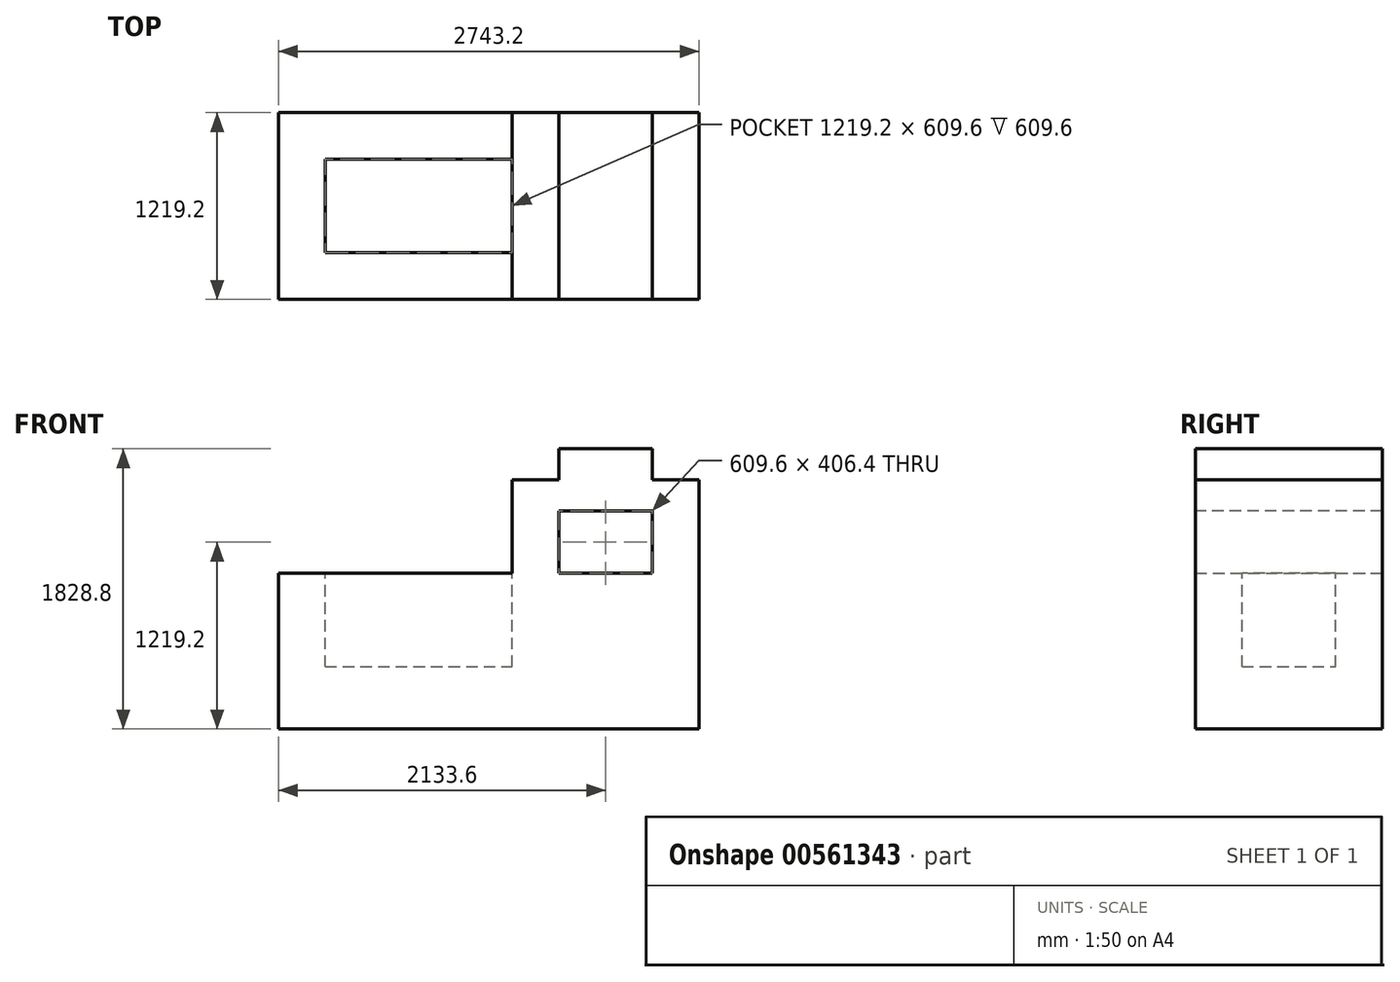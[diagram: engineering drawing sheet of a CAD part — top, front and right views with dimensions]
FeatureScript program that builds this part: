
annotation { "Feature Type Name" : "Feature", "Feature Type Description" : "" }
export const myFeature = defineFeature(function(context is Context, id is Id, definition is map)
    precondition{}
    {
        {
            var Q0;
            Q0=qCreatedBy(makeId("Front.planeOp"),FACE);
            var sketch = newSketch(context, id + "F0", { "sketchPlane" : qUnion([Q0])});
            skLineSegment(sketch, "E0", {"start": v(-76.3, -75.97) * mm, "end": v(2666.9, -75.97) * mm});
            skLineSegment(sketch, "E1", {"start": v(2666.9, -75.97) * mm, "end": v(2666.9, 1549.63) * mm});
            skLineSegment(sketch, "E2", {"start": v(2666.9, 1549.63) * mm, "end": v(2362.1, 1549.63) * mm});
            skLineSegment(sketch, "E3", {"start": v(2362.1, 1549.63) * mm, "end": v(2362.1, 1752.83) * mm});
            skLineSegment(sketch, "E4", {"start": v(2362.1, 1752.83) * mm, "end": v(1752.5, 1752.83) * mm});
            skLineSegment(sketch, "E5", {"start": v(1752.5, 1752.83) * mm, "end": v(1752.5, 1549.63) * mm});
            skLineSegment(sketch, "E6", {"start": v(1752.5, 1549.63) * mm, "end": v(1447.7, 1549.63) * mm});
            skLineSegment(sketch, "E7", {"start": v(1447.7, 1549.63) * mm, "end": v(1447.7, 940.03) * mm});
            skLineSegment(sketch, "E8", {"start": v(1447.7, 940.03) * mm, "end": v(-76.3, 940.03) * mm});
            skLineSegment(sketch, "E9", {"start": v(-76.3, 940.03) * mm, "end": v(-76.3, -75.97) * mm});
            skLineSegment(sketch, "E10", {"start": v(1752.5, 940.03) * mm, "end": v(2362.1, 940.03) * mm});
            skLineSegment(sketch, "E11", {"start": v(2362.1, 940.03) * mm, "end": v(2362.1, 1346.43) * mm});
            skLineSegment(sketch, "E12", {"start": v(2362.1, 1346.43) * mm, "end": v(1752.5, 1346.43) * mm});
            skLineSegment(sketch, "E13", {"start": v(1752.5, 1346.43) * mm, "end": v(1752.5, 940.03) * mm});
            skSolve(sketch);
        }
        {
            var Q0;
            Q0=makeQuery(id+"F0.imprint","IMPRINT",FACE,{"disambiguationData":[TD([[makeQuery(id+"F0.imprint","IMPRINT",EDGE,{"derivedFrom":sQuery(id+"F0.wireOp",EDGE,"E0")}),1.0]])]});
            var Q1;
            Q1=makeQuery(id+"F0.imprint","IMPRINT",FACE,{"disambiguationData":[TD([[makeQuery(id+"F0.imprint","IMPRINT",EDGE,{"derivedFrom":sQuery(id+"F0.wireOp",EDGE,"E10")}),1.0]])]});
            extrude(context, id + "F1", {"entities" : qUnion([Q0, Q1]), "depth" : 1219.2 * mm, "offsetDistance" : 25.4 * mm});
        }
        {
            var Q0;
            Q0=makeQuery(id+"F1.opExtrude","CAP_FACE",FACE,{"disambiguationData":[OSD([sQuery(id+"F0.wireOp",EDGE,"E0"),sQuery(id+"F0.wireOp",EDGE,"E1"),sQuery(id+"F0.wireOp",EDGE,"E2"),sQuery(id+"F0.wireOp",EDGE,"E3"),sQuery(id+"F0.wireOp",EDGE,"E4"),sQuery(id+"F0.wireOp",EDGE,"E5"),sQuery(id+"F0.wireOp",EDGE,"E6"),sQuery(id+"F0.wireOp",EDGE,"E7"),sQuery(id+"F0.wireOp",EDGE,"E8"),sQuery(id+"F0.wireOp",EDGE,"E9")])],"isStart":false});
            var sketch = newSketch(context, id + "F2", { "sketchPlane" : qUnion([Q0])});
            skLineSegment(sketch, "E14", {"start": v(1752.5, 940.03) * mm, "end": v(2362.1, 940.03) * mm});
            skLineSegment(sketch, "E15", {"start": v(2362.1, 940.03) * mm, "end": v(2362.1, 1346.43) * mm});
            skLineSegment(sketch, "E16", {"start": v(2362.1, 1346.43) * mm, "end": v(1752.5, 1346.43) * mm});
            skLineSegment(sketch, "E17", {"start": v(1752.5, 1346.43) * mm, "end": v(1752.5, 940.03) * mm});
            skSolve(sketch);
        }
        {
            var Q0;
            Q0=makeQuery(id+"F2.imprint","IMPRINT",FACE,{"disambiguationData":[TD([[makeQuery(id+"F2.imprint","IMPRINT",EDGE,{"derivedFrom":sQuery(id+"F2.wireOp",EDGE,"E14")}),1.0]])]});
            extrude(context, id + "F3", {"entities" : qUnion([Q0]), "operationType" : NewBodyOperationType.REMOVE, "endBound" : BoundingType.THROUGH_ALL, "oppositeDirection" : true, "depth" : 25.4 * mm, "offsetDistance" : 25.4 * mm});
        }
        {
            var Q0;
            Q0=makeQuery(id+"F1.opExtrude","SWEPT_FACE",FACE,{"disambiguationData":[OSD([sQuery(id+"F0.wireOp",EDGE,"E8")])]});
            var sketch = newSketch(context, id + "F4", { "sketchPlane" : qUnion([Q0])});
            skLineSegment(sketch, "E18", {"start": v(-76.3, -1219.2) * mm, "end": v(-76.3, -914.4) * mm});
            skLineSegment(sketch, "E19", {"start": v(-76.3, -914.4) * mm, "end": v(1447.7, -914.4) * mm});
            skLineSegment(sketch, "E20", {"start": v(1447.7, -914.4) * mm, "end": v(1447.7, 0) * mm});
            skLineSegment(sketch, "E21", {"start": v(1447.7, 0) * mm, "end": v(-76.3, 0) * mm});
            skLineSegment(sketch, "E22", {"start": v(-76.3, 0) * mm, "end": v(-76.3, -304.8) * mm});
            skLineSegment(sketch, "E23", {"start": v(-76.3, -304.8) * mm, "end": v(1447.7, -304.8) * mm});
            skLineSegment(sketch, "E24", {"start": v(-76.3, -609.6) * mm, "end": v(228.5, -609.6) * mm});
            skLineSegment(sketch, "E25", {"start": v(228.5, -609.6) * mm, "end": v(228.5, -914.4) * mm});
            skLineSegment(sketch, "E26", {"start": v(228.5, -914.4) * mm, "end": v(228.5, -304.8) * mm});
            skPoint(sketch, "E26.endSnap0", {"position": v(228.5, -762) * mm});
            skSolve(sketch);
        }
        {
            var Q0;
            {var subQ4=sQuery(id+"F4.wireOp",EDGE,"E23");var subQ5=sQuery(id+"F4.wireOp",EDGE,"E20");var subQ6=makeQuery(id+"F4.imprint","INTERSECT",VERTEX,{"derivedFrom":[subQ5,subQ4]});Q0=makeQuery(id+"F4.imprint","IMPRINT",FACE,{"disambiguationData":[TD([[makeQuery(id+"F4.imprint","IMPRINT",EDGE,{"disambiguationData":[TD([[subQ6,1.0]])],"derivedFrom":subQ4}),-1.0]])]});}
            extrude(context, id + "F5", {"entities" : qUnion([Q0]), "operationType" : NewBodyOperationType.REMOVE, "oppositeDirection" : true, "depth" : 609.6 * mm, "offsetDistance" : 25.4 * mm});
        }
    });
